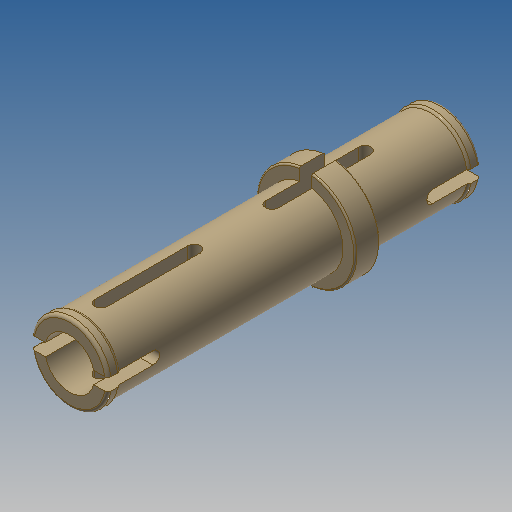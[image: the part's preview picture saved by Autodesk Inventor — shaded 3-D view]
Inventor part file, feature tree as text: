
AUTODESK INVENTOR PART (.ipt)
format: ipt  version: 2022.2 (Build 262287000, 287)  size: 300,032 bytes
history: native  units: mm (DEFAULTED — no unit token found)
features: sketch x2, extrude x2, revolve x1, fillet x1
ambient origin geometry x8: Origin, YZ Plane, XZ Plane, XY Plane, X Axis, Y Axis, Z Axis, Center Point
bodies: Solid2 (feature_tree)
feature tree (6):
  sketch  "Sketch1"  dims[d1=4.8mm d2=5.0mm d6=16.0mm]
  revolve  "Revolution1"  [1 undecoded]
  fillet  "Fillet1"  Radius=16.0mm
  extrude  "Extrusion1"  Depth=0.8mm
  extrude  "Extrusion2"  Depth=0.8mm
  sketch  "Sketch2"  dims[d7=0.8mm d8=6.4mm d9=0.8mm d10=0.8mm d14=0.8mm d16=6.8mm d17=0.8mm d18=2.0mm d19=8.0mm d20=90.0deg d21=10.0mm d22=0.0mm d25=10.0mm d26=0.0mm d27=0.2mm d28=0.1mm d29=0.0mm d30=0.0mm d31=3.2mm d32=3.4mm d33=0.8mm d34=3.4mm]
note: 1 required parameter value undecoded (feature->parameter linkage not recoverable at this tier; creation-order binding heuristic only, values carry confidence <= 0.55)
